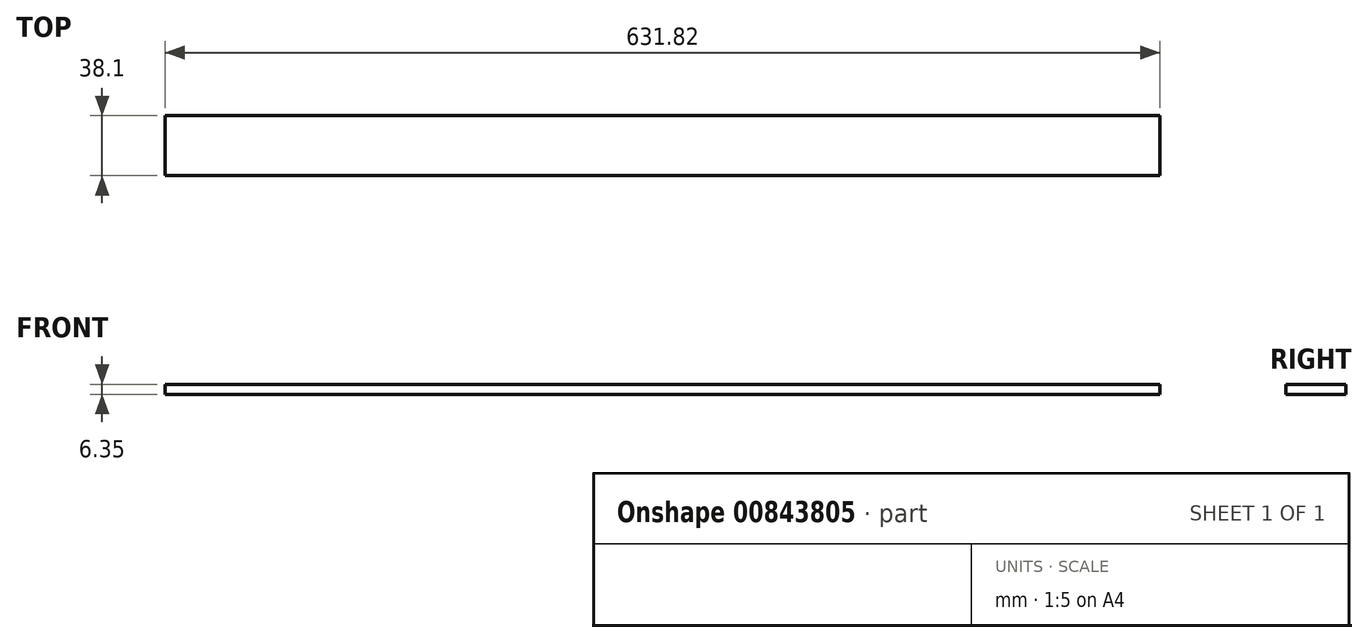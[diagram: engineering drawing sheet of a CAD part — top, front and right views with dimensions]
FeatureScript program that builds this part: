
annotation { "Feature Type Name" : "Feature", "Feature Type Description" : "" }
export const myFeature = defineFeature(function(context is Context, id is Id, definition is map)
    precondition{}
    {
        {
            var Q0;
            Q0=qCreatedBy(makeId("Top.planeOp"),FACE);
            var sketch = newSketch(context, id + "F0", { "sketchPlane" : qUnion([Q0])});
            skLineSegment(sketch, "E0.bottom", {"start": v(315.91, 19.05) * mm, "end": v(-315.91, 19.05) * mm});
            skLineSegment(sketch, "E0.top", {"start": v(315.91, -19.05) * mm, "end": v(-315.91, -19.05) * mm});
            skLineSegment(sketch, "E0.left", {"start": v(315.91, 19.05) * mm, "end": v(315.91, -19.05) * mm});
            skLineSegment(sketch, "E0.right", {"start": v(-315.91, 19.05) * mm, "end": v(-315.91, -19.05) * mm});
            skPoint(sketch, "E0.middle", {"position": v(0, 0) * mm});
            skSolve(sketch);
        }
        {
            var Q0;
            Q0 = qSketchRegion(id + "F0", true);
            extrude(context, id + "F1", {"entities" : qUnion([Q0]), "depth" : 6.35 * mm, "offsetDistance" : 25.4 * mm});
        }
    });
